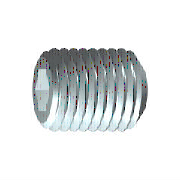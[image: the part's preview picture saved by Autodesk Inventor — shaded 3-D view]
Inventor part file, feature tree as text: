
AUTODESK INVENTOR PART (.ipt)
format: ipt  version: 2014 (Build 180170000, 170)  size: 168,960 bytes
history: native  units: mm (DEFAULTED — no unit token found)
features: sketch x2, extrude x1, other x1, plane x1
ambient origin geometry x8: Origin, YZ Plane, XZ Plane, XY Plane, X Axis, Y Axis, Z Axis, Center Point
bodies: Solid1 (feature_tree), Body (feature_tree)
feature tree (5):
  extrude  "Slot"  TaperAngle=60.0deg  [1 undecoded]
  other  "Work Axis1"
  plane  "Work Plane1"
  sketch  "Sketch1"  dims[d0=3.175mm d1=60.0deg]
  sketch  "Sketch2"  dims[d2=6.35mm d3=3.666174mm d6=90.0deg d4=0.0mm d5=6.35mm d7=0.779062mm d8=45.0deg d21=10.0mm d9=0.0mm d11=6.35mm d12=0.0mm d13=0.779062mm d14=45.0deg d15=0.0mm d29=0.779062mm d30=0.779062mm d31=0.0mm]
note: 1 required parameter value undecoded (feature->parameter linkage not recoverable at this tier; creation-order binding heuristic only, values carry confidence <= 0.55)
